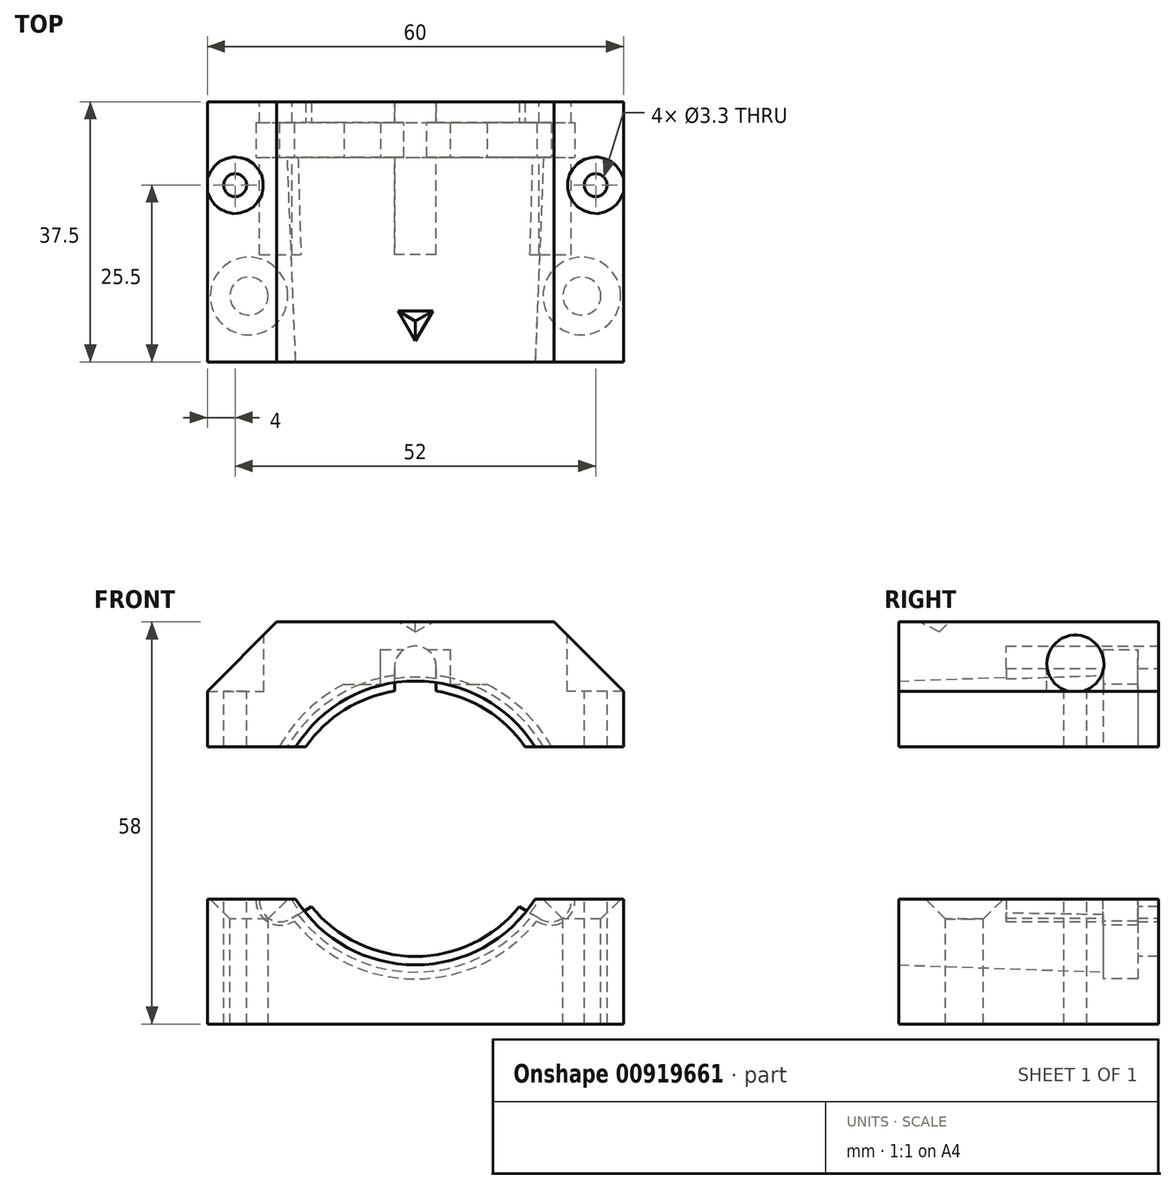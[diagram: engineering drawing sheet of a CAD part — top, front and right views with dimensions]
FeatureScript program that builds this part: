
annotation { "Feature Type Name" : "Feature", "Feature Type Description" : "" }
export const myFeature = defineFeature(function(context is Context, id is Id, definition is map)
    precondition{}
    {
        {
            var Q0;
            Q0=qCreatedBy(makeId("Front.planeOp"),FACE);
            var sketch = newSketch(context, id + "F0", { "sketchPlane" : qUnion([Q0])});
            skCircle(sketch, "E0", {"center": v(0, 0) * mm, "radius": 22.5 * mm, "construction": true});
            skLineSegment(sketch, "E1.bottom", {"start": v(5, 20) * mm, "end": v(-5, 20) * mm, "construction": true});
            skLineSegment(sketch, "E1.top", {"start": v(5, 25) * mm, "end": v(-5, 25) * mm, "construction": true});
            skLineSegment(sketch, "E1.left", {"start": v(5, 20) * mm, "end": v(5, 25) * mm, "construction": true});
            skLineSegment(sketch, "E1.right", {"start": v(-5, 20) * mm, "end": v(-5, 25) * mm, "construction": true});
            skPoint(sketch, "E1.middle", {"position": v(0, 22.5) * mm});
            skCircle(sketch, "E2", {"center": v(-19.49, -11.25) * mm, "radius": 3.5 * mm, "construction": true});
            skCircle(sketch, "E3.MirrorC", {"center": v(19.49, -11.25) * mm, "radius": 3.5 * mm, "construction": true});
            skLineSegment(sketch, "E4", {"start": v(-19.49, -11.25) * mm, "end": v(0, 0) * mm, "construction": true});
            skLineSegment(sketch, "E5", {"start": v(-10.3, 20) * mm, "end": v(-5, 20) * mm});
            skLineSegment(sketch, "E6", {"start": v(-5, 25) * mm, "end": v(5, 25) * mm});
            skLineSegment(sketch, "E7", {"start": v(5, 20) * mm, "end": v(10.3, 20) * mm});
            skArc(sketch, "E8", {"start": v(10.3, 20) * mm, "mid": v(21.03, 8) * mm, "end": v(21, -8.1) * mm});
            skArc(sketch, "E9", {"start": v(21, -8.1) * mm, "mid": v(22.52, -13) * mm, "end": v(17.5, -14.14) * mm});
            skArc(sketch, "E10", {"start": v(17.5, -14.14) * mm, "mid": v(0, -22.5) * mm, "end": v(-17.5, -14.14) * mm});
            skArc(sketch, "E11", {"start": v(-17.5, -14.14) * mm, "mid": v(-22.52, -13) * mm, "end": v(-21, -8.1) * mm});
            skArc(sketch, "E12", {"start": v(-21, -8.1) * mm, "mid": v(-21.03, 8) * mm, "end": v(-10.3, 20) * mm});
            skLineSegment(sketch, "E13", {"start": v(-5, 20) * mm, "end": v(-5, 25) * mm});
            skLineSegment(sketch, "E14", {"start": v(5, 25) * mm, "end": v(5, 20) * mm});
            skSolve(sketch);
        }
        {
            var Q0;
            Q0=qCreatedBy(makeId("Front.planeOp"),FACE);
            var sketch = newSketch(context, id + "F1", { "sketchPlane" : qUnion([Q0])});
            skLineSegment(sketch, "E15.bottom", {"start": v(-30, -29) * mm, "end": v(30, -29) * mm});
            skLineSegment(sketch, "E15.top", {"start": v(-30, -11) * mm, "end": v(30, -11) * mm});
            skLineSegment(sketch, "E15.left", {"start": v(-30, -29) * mm, "end": v(-30, -11) * mm});
            skLineSegment(sketch, "E15.right", {"start": v(30, -29) * mm, "end": v(30, -11) * mm});
            skLineSegment(sketch, "E16.bottom", {"start": v(-30, 11) * mm, "end": v(30, 11) * mm});
            skLineSegment(sketch, "E16.left", {"start": v(-30, 11) * mm, "end": v(-30, 29) * mm});
            skLineSegment(sketch, "E16.right", {"start": v(30, 11) * mm, "end": v(30, 29) * mm});
            skLineSegment(sketch, "E17", {"start": v(-30, 29) * mm, "end": v(30, 29) * mm});
            skSolve(sketch);
        }
        {
            var Q0;
            Q0 = qSketchRegion(id + "F1", true);
            extrude(context, id + "F2", {"entities" : qUnion([Q0]), "depth" : 29.5 * mm, "offsetDistance" : 25 * mm, "hasSecondDirection" : true, "secondDirectionOppositeDirection" : true, "secondDirectionDepth" : 8 * mm});
        }
        {
            var Q0;
            Q0 = qSketchRegion(id + "F0", true);
            extrude(context, id + "F3", {"entities" : qUnion([Q0]), "operationType" : NewBodyOperationType.REMOVE, "oppositeDirection" : true, "depth" : 5 * mm, "offsetDistance" : 25 * mm});
        }
        {
            var Q0;
            Q0=qCreatedBy(makeId("Front.planeOp"),FACE);
            var sketch = newSketch(context, id + "F4", { "sketchPlane" : qUnion([Q0])});
            skCircle(sketch, "E18", {"center": v(0, 0) * mm, "radius": 19.25 * mm});
            skSolve(sketch);
        }
        {
            var Q0;
            Q0 = qSketchRegion(id + "F4", true);
            extrude(context, id + "F5", {"entities" : qUnion([Q0]), "operationType" : NewBodyOperationType.REMOVE, "oppositeDirection" : true, "depth" : 25 * mm, "offsetDistance" : 25 * mm});
        }
        {
            var Q0;
            Q0=qCreatedBy(makeId("Front.planeOp"),FACE);
            var sketch = newSketch(context, id + "F6", { "sketchPlane" : qUnion([Q0])});
            skCircle(sketch, "E19", {"center": v(0, 0) * mm, "radius": 21.5 * mm});
            skSolve(sketch);
        }
        {
            var Q0;
            Q0 = qSketchRegion(id + "F6", true);
            extrude(context, id + "F7", {"entities" : qUnion([Q0]), "operationType" : NewBodyOperationType.REMOVE, "depth" : 30 * mm, "offsetDistance" : 25 * mm, "hasDraft" : true, "draftAngle" : 2 * degree, "draftPullDirection" : true});
        }
        {
            var Q0;
            Q0=qCreatedBy(makeId("Front.planeOp"),FACE);
            var sketch = newSketch(context, id + "F8", { "sketchPlane" : qUnion([Q0])});
            skPoint(sketch, "E20.center", {"position": v(0, 0) * mm});
            skLineSegment(sketch, "E21", {"start": v(-3, 22.3) * mm, "end": v(-3, 16.31) * mm});
            skLineSegment(sketch, "E22", {"start": v(-3, 16.31) * mm, "end": v(3, 16.31) * mm});
            skLineSegment(sketch, "E23", {"start": v(3, 16.31) * mm, "end": v(3, 22.3) * mm});
            skArc(sketch, "E24", {"start": v(-3, 22.3) * mm, "mid": v(0, 25.5) * mm, "end": v(3, 22.3) * mm});
            skLineSegment(sketch, "E25.1.0", {"start": v(20.8, -8.56) * mm, "end": v(15.62, -5.56) * mm});
            skArc(sketch, "E25.1.1", {"start": v(20.8, -8.56) * mm, "mid": v(22.08, -12.75) * mm, "end": v(17.82, -13.74) * mm});
            skLineSegment(sketch, "E25.1.2", {"start": v(12.63, -10.75) * mm, "end": v(17.82, -13.74) * mm});
            skLineSegment(sketch, "E25.1.3", {"start": v(15.62, -5.56) * mm, "end": v(12.63, -10.75) * mm});
            skLineSegment(sketch, "E25.2.0", {"start": v(-17.82, -13.74) * mm, "end": v(-12.63, -10.75) * mm});
            skArc(sketch, "E25.2.1", {"start": v(-17.82, -13.74) * mm, "mid": v(-22.08, -12.75) * mm, "end": v(-20.8, -8.56) * mm});
            skLineSegment(sketch, "E25.2.2", {"start": v(-15.62, -5.56) * mm, "end": v(-20.8, -8.56) * mm});
            skLineSegment(sketch, "E25.2.3", {"start": v(-12.63, -10.75) * mm, "end": v(-15.62, -5.56) * mm});
            skLineSegment(sketch, "E25.anchor1", {"start": v(0, 0) * mm, "end": v(-3, 16.31) * mm, "construction": true});
            skLineSegment(sketch, "E25.anchor2", {"start": v(0, 0) * mm, "end": v(-12.63, -10.75) * mm, "construction": true});
            skSolve(sketch);
        }
        {
            var Q0;
            Q0 = qSketchRegion(id + "F8", true);
            extrude(context, id + "F9", {"entities" : qUnion([Q0]), "operationType" : NewBodyOperationType.REMOVE, "endBound" : BoundingType.SYMMETRIC, "depth" : 28 * mm, "offsetDistance" : 25 * mm, "hasSecondDirection" : true, "secondDirectionOppositeDirection" : true, "secondDirectionDepth" : 14 * mm});
        }
        {
            var Q0;
            Q0=makeQuery(id+"F2.opExtrude","SWEPT_FACE",FACE,{"disambiguationData":[OSD([sQuery(id+"F1.wireOp",EDGE,"E17")])]});
            var sketch = newSketch(context, id + "F10", { "sketchPlane" : qUnion([Q0])});
            skLineSegment(sketch, "E26", {"start": v(0, -26.5) * mm, "end": v(-2.5, -22.17) * mm});
            skLineSegment(sketch, "E27", {"start": v(-2.5, -22.17) * mm, "end": v(2.5, -22.17) * mm});
            skLineSegment(sketch, "E28", {"start": v(2.5, -22.17) * mm, "end": v(0, -26.5) * mm});
            skSolve(sketch);
        }
        {
            var Q0;
            Q0 = qSketchRegion(id + "F10", true);
            extrude(context, id + "F11", {"entities" : qUnion([Q0]), "operationType" : NewBodyOperationType.REMOVE, "oppositeDirection" : true, "depth" : 2 * mm, "offsetDistance" : 25 * mm, "hasDraft" : true, "draftAngle" : 45 * degree, "draftPullDirection" : true});
        }
        {
            var Q0;
            Q0=makeQuery(id+"F2.opExtrude","SWEPT_EDGE",EDGE,{"disambiguationData":[OSD([sQuery(id+"F1.wireOp",EDGE,"E16.right"),sQuery(id+"F1.wireOp",EDGE,"E17")])]});
            var Q1;
            Q1=makeQuery(id+"F2.opExtrude","SWEPT_EDGE",EDGE,{"disambiguationData":[OSD([sQuery(id+"F1.wireOp",EDGE,"E16.left"),sQuery(id+"F1.wireOp",EDGE,"E17")])]});
            chamfer(context, id + "F12", {"entities" : qUnion([Q0, Q1]), "width" : 10 * mm, "tangentPropagation" : true});
        }
        {
            var Q0;
            {var subQ2=sQuery(id+"F1.wireOp",EDGE,"E15.left");var subQ4=sQuery(id+"F1.wireOp",EDGE,"E15.top");var subQ7=makeQuery(id+"F2.opExtrude","SWEPT_FACE",FACE,{"disambiguationData":[OSD([subQ4])]});Q0=makeQuery(id+"F7.boolean.opBoolean","SPLIT",FACE,{"disambiguationData":[TD([makeQuery(id+"F2.opExtrude","SWEPT_FACE",FACE,{"disambiguationData":[OSD([subQ2])]})])],"derivedFrom":subQ7});}
            var sketch = newSketch(context, id + "F13", { "sketchPlane" : qUnion([Q0])});
            skLineSegment(sketch, "E29", {"start": v(-24, -20) * mm, "end": v(24, -20) * mm, "construction": true});
            skSolve(sketch);
        }
        {
            var Q0;
            Q0=sQuery(id+"F13.wireOp",VERTEX,"E29.start");
            var Q1;
            Q1=sQuery(id+"F13.wireOp",VERTEX,"E29.end");
            var Q2;
            Q2=makeQuery(id+"F2.opExtrude","SWEPT_BODY",BODY,{"disambiguationData":[OSD([sQuery(id+"F1.wireOp",EDGE,"E15.bottom"),sQuery(id+"F1.wireOp",EDGE,"E15.top"),sQuery(id+"F1.wireOp",EDGE,"E15.left"),sQuery(id+"F1.wireOp",EDGE,"E15.right")])]});
            hole(context, id + "F14", {"style" : HoleStyle.C_SINK, "endStyle" : HoleEndStyle.BLIND, "standardTappedOrClearance" : lookupTablePath({ "fit" : "Normal", "standard" : "ISO", "size" : "M5", "type" : "Clearance" }), "standardBlindInLast" : lookupTablePath({ "fit" : "Normal", "standard" : "ISO", "engagement" : "75%", "pitch" : "0.8 mm", "size" : "M5", "type" : "Clearance & tapped" }), "holeDiameter" : 5.5 * mm, "cSinkDiameter" : 11.2 * mm, "cSinkAngle" : 90 * degree, "majorDiameter" : 5 * mm, "holeDepth" : 40 * mm, "isTappedThrough" : true, "tappedDepth" : 12 * mm, "tapClearance" : 3, "locations" : qUnion([Q0, Q1]), "scope" : qUnion([Q2])});
        }
        {
            var Q0;
            Q0=makeQuery(id+"F2.opExtrude","SWEPT_FACE",FACE,{"disambiguationData":[OSD([sQuery(id+"F1.wireOp",EDGE,"E17")])]});
            var sketch = newSketch(context, id + "F15", { "sketchPlane" : qUnion([Q0])});
            skLineSegment(sketch, "E30", {"start": v(-26, -4) * mm, "end": v(26, -4) * mm, "construction": true});
            skSolve(sketch);
        }
        {
            var Q0;
            Q0=sQuery(id+"F15.wireOp",VERTEX,"E30.start");
            var Q1;
            Q1=sQuery(id+"F15.wireOp",VERTEX,"E30.end");
            var Q2;
            Q2=makeQuery(id+"F2.opExtrude","SWEPT_BODY",BODY,{"disambiguationData":[OSD([sQuery(id+"F1.wireOp",EDGE,"E15.bottom"),sQuery(id+"F1.wireOp",EDGE,"E15.top"),sQuery(id+"F1.wireOp",EDGE,"E15.left"),sQuery(id+"F1.wireOp",EDGE,"E15.right")])]});
            var Q3;
            Q3=makeQuery(id+"F2.opExtrude","SWEPT_BODY",BODY,{"disambiguationData":[OSD([sQuery(id+"F1.wireOp",EDGE,"E16.bottom"),sQuery(id+"F1.wireOp",EDGE,"E16.left"),sQuery(id+"F1.wireOp",EDGE,"E16.right"),sQuery(id+"F1.wireOp",EDGE,"E17")])]});
            hole(context, id + "F16", {"style" : HoleStyle.C_BORE, "endStyle" : HoleEndStyle.BLIND, "holeDiameter" : 3.3 * mm, "cBoreDiameter" : 8.25 * mm, "cBoreDepth" : 10 * mm, "majorDiameter" : 4 * mm, "holeDepth" : 58 * mm, "isTappedThrough" : true, "tappedDepth" : 60 * mm, "tapClearance" : 3, "startFromSketch" : true, "locations" : qUnion([Q0, Q1]), "scope" : qUnion([Q2, Q3])});
        }
    });
